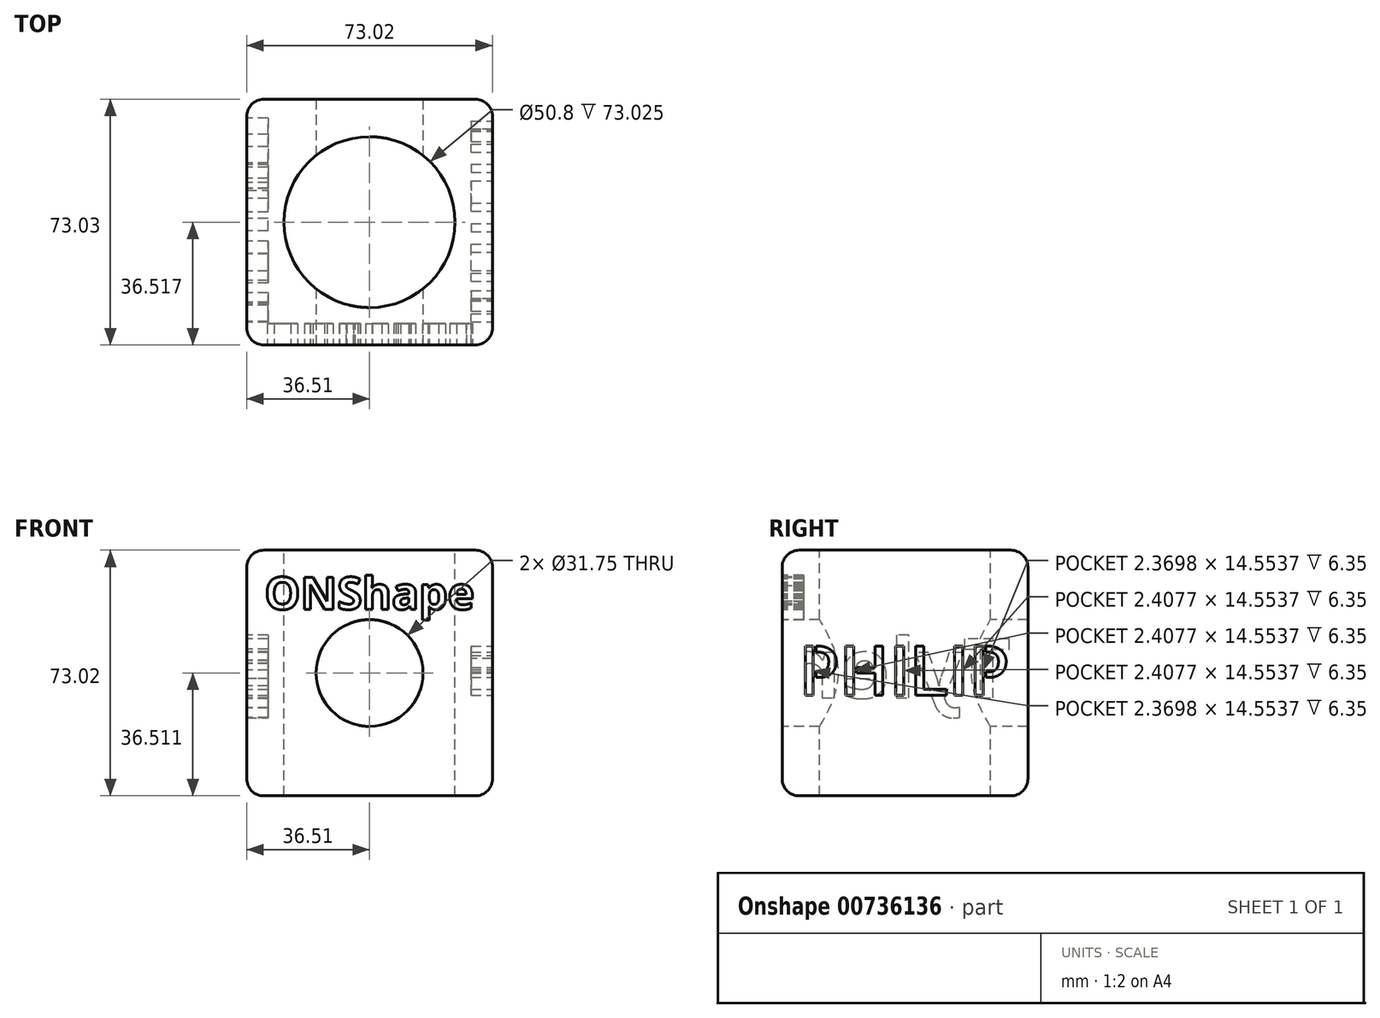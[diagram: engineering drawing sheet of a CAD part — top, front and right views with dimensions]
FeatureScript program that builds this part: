
annotation { "Feature Type Name" : "Feature", "Feature Type Description" : "" }
export const myFeature = defineFeature(function(context is Context, id is Id, definition is map)
    precondition{}
    {
        {
            var Q0;
            Q0=qCreatedBy(makeId("Front.planeOp"),FACE);
            var sketch = newSketch(context, id + "F0", { "sketchPlane" : qUnion([Q0])});
            skLineSegment(sketch, "E0", {"start": v(-67.88, -21.03) * mm, "end": v(5.14, -21.03) * mm});
            skLineSegment(sketch, "E1", {"start": v(5.14, -21.03) * mm, "end": v(5.14, 52) * mm});
            skLineSegment(sketch, "E2", {"start": v(5.14, 52) * mm, "end": v(-67.88, 52) * mm});
            skLineSegment(sketch, "E3", {"start": v(-67.88, 52) * mm, "end": v(-67.88, -21.03) * mm});
            skSolve(sketch);
        }
        {
            var Q0;
            Q0=makeQuery(id+"F0.imprint","IMPRINT",FACE,{"disambiguationData":[TD([[makeQuery(id+"F0.imprint","IMPRINT",EDGE,{"derivedFrom":sQuery(id+"F0.wireOp",EDGE,"E0")}),1.0]])]});
            extrude(context, id + "F1", {"entities" : qUnion([Q0]), "depth" : 73.02 * mm, "offsetDistance" : 25.4 * mm});
        }
        {
            var Q0;
            Q0=makeQuery(id+"F1.opExtrude","SWEPT_FACE",FACE,{"disambiguationData":[OSD([sQuery(id+"F0.wireOp",EDGE,"E2")])]});
            var Q1;
            Q1=makeQuery(id+"F1.opExtrude","SWEPT_FACE",FACE,{"disambiguationData":[OSD([sQuery(id+"F0.wireOp",EDGE,"E1")])]});
            var Q2;
            Q2=makeQuery(id+"F1.opExtrude","CAP_FACE",FACE,{"disambiguationData":[OSD([sQuery(id+"F0.wireOp",EDGE,"E0"),sQuery(id+"F0.wireOp",EDGE,"E1"),sQuery(id+"F0.wireOp",EDGE,"E2"),sQuery(id+"F0.wireOp",EDGE,"E3")])],"isStart":false});
            var Q3;
            Q3=makeQuery(id+"F1.opExtrude","SWEPT_FACE",FACE,{"disambiguationData":[OSD([sQuery(id+"F0.wireOp",EDGE,"E0")])]});
            var Q4;
            Q4=makeQuery(id+"F1.opExtrude","CAP_FACE",FACE,{"disambiguationData":[OSD([sQuery(id+"F0.wireOp",EDGE,"E0"),sQuery(id+"F0.wireOp",EDGE,"E1"),sQuery(id+"F0.wireOp",EDGE,"E2"),sQuery(id+"F0.wireOp",EDGE,"E3")])],"isStart":true});
            fillet(context, id + "F2", {"entities" : qUnion([Q0, Q1, Q2, Q3, Q4]), "radius" : 5.08 * mm, "tangentPropagation" : true, "allowEdgeOverflow" : false});
        }
        {
            var Q0;
            Q0=makeQuery(id+"F1.opExtrude","SWEPT_FACE",FACE,{"disambiguationData":[OSD([sQuery(id+"F0.wireOp",EDGE,"E2")])]});
            var sketch = newSketch(context, id + "F3", { "sketchPlane" : qUnion([Q0])});
            skPoint(sketch, "E4", {"position": v(-31.37, -36.51) * mm});
            skSolve(sketch);
        }
        {
            var Q0;
            Q0=sQuery(id+"F3.wireOp",VERTEX,"E4");
            var Q1;
            Q1=makeQuery(id+"F1.opExtrude","SWEPT_BODY",BODY,{"disambiguationData":[OSD([sQuery(id+"F0.wireOp",EDGE,"E0"),sQuery(id+"F0.wireOp",EDGE,"E1"),sQuery(id+"F0.wireOp",EDGE,"E2"),sQuery(id+"F0.wireOp",EDGE,"E3")])]});
            hole(context, id + "F4", {"style" : HoleStyle.SIMPLE, "endStyle" : HoleEndStyle.THROUGH, "holeDiameter" : 50.8 * mm, "majorDiameter" : 6.35 * mm, "isTappedThrough" : true, "tappedDepth" : 12.7 * mm, "tapClearance" : 3, "locations" : qUnion([Q0]), "scope" : qUnion([Q1])});
        }
        {
            var Q0;
            Q0=makeQuery(id+"F1.opExtrude","CAP_FACE",FACE,{"disambiguationData":[OSD([sQuery(id+"F0.wireOp",EDGE,"E0"),sQuery(id+"F0.wireOp",EDGE,"E1"),sQuery(id+"F0.wireOp",EDGE,"E2"),sQuery(id+"F0.wireOp",EDGE,"E3")])],"isStart":false});
            var sketch = newSketch(context, id + "F5", { "sketchPlane" : qUnion([Q0])});
            skPoint(sketch, "E5", {"position": v(-31.37, 15.48) * mm});
            skSolve(sketch);
        }
        {
            var Q0;
            Q0=sQuery(id+"F5.wireOp",VERTEX,"E5");
            var Q1;
            Q1=makeQuery(id+"F1.opExtrude","SWEPT_BODY",BODY,{"disambiguationData":[OSD([sQuery(id+"F0.wireOp",EDGE,"E0"),sQuery(id+"F0.wireOp",EDGE,"E1"),sQuery(id+"F0.wireOp",EDGE,"E2"),sQuery(id+"F0.wireOp",EDGE,"E3")])]});
            hole(context, id + "F6", {"style" : HoleStyle.SIMPLE, "endStyle" : HoleEndStyle.THROUGH, "holeDiameter" : 31.75 * mm, "majorDiameter" : 6.35 * mm, "isTappedThrough" : true, "tappedDepth" : 12.7 * mm, "tapClearance" : 3, "locations" : qUnion([Q0]), "scope" : qUnion([Q1])});
        }
        {
            var Q0;
            Q0=makeQuery(id+"F1.opExtrude","CAP_FACE",FACE,{"disambiguationData":[OSD([sQuery(id+"F0.wireOp",EDGE,"E0"),sQuery(id+"F0.wireOp",EDGE,"E1"),sQuery(id+"F0.wireOp",EDGE,"E2"),sQuery(id+"F0.wireOp",EDGE,"E3")])],"isStart":false});
            var sketch = newSketch(context, id + "F7", { "sketchPlane" : qUnion([Q0])});
            skText(sketch, "E6", { "text": "ONShape", "fontName": "OpenSans-Bold.ttf"});
            skPoint(sketch, "E7", {"position": v(-31.37, 46.91) * mm});
            const initialGuessF7  = {"E6": [-0.0626, 0.03439, 1, 0, 0.00967]};
            skSetInitialGuess(sketch, initialGuessF7);
            skSolve(sketch);
        }
        {
            var Q0;
            Q0 = qSketchRegion(id + "F7", true);
            extrude(context, id + "F8", {"entities" : qUnion([Q0]), "operationType" : NewBodyOperationType.REMOVE, "oppositeDirection" : true, "depth" : 6.35 * mm, "offsetDistance" : 25.4 * mm});
        }
        {
            var Q0;
            Q0=makeQuery(id+"F1.opExtrude","SWEPT_FACE",FACE,{"disambiguationData":[OSD([sQuery(id+"F0.wireOp",EDGE,"E1")])]});
            var sketch = newSketch(context, id + "F9", { "sketchPlane" : qUnion([Q0])});
            skText(sketch, "E8", { "text": "PHILIP", "fontName": "AllertaStencil-Regular.ttf"});
            const initialGuessF9  = {"E8": [-0.06795, 0.00889, 1, 0, 0.01456]};
            skSetInitialGuess(sketch, initialGuessF9);
            skSolve(sketch);
        }
        {
            var Q0;
            Q0 = qSketchRegion(id + "F9", true);
            extrude(context, id + "F10", {"entities" : qUnion([Q0]), "operationType" : NewBodyOperationType.REMOVE, "oppositeDirection" : true, "depth" : 6.35 * mm, "offsetDistance" : 25.4 * mm});
        }
        {
            var Q0;
            Q0=makeQuery(id+"F1.opExtrude","SWEPT_FACE",FACE,{"disambiguationData":[OSD([sQuery(id+"F0.wireOp",EDGE,"E3")])]});
            var sketch = newSketch(context, id + "F11", { "sketchPlane" : qUnion([Q0])});
            skText(sketch, "E9", { "text": "Tyler", "fontName": "NotoSans-Bold.ttf"});
            const initialGuessF11  = {"E9": [0.00508, 0.00804, 1, 0, 0.0178]};
            skSetInitialGuess(sketch, initialGuessF11);
            skSolve(sketch);
        }
        {
            var Q0;
            Q0 = qSketchRegion(id + "F11", true);
            extrude(context, id + "F12", {"entities" : qUnion([Q0]), "operationType" : NewBodyOperationType.REMOVE, "oppositeDirection" : true, "depth" : 6.35 * mm, "offsetDistance" : 25.4 * mm});
        }
    });
